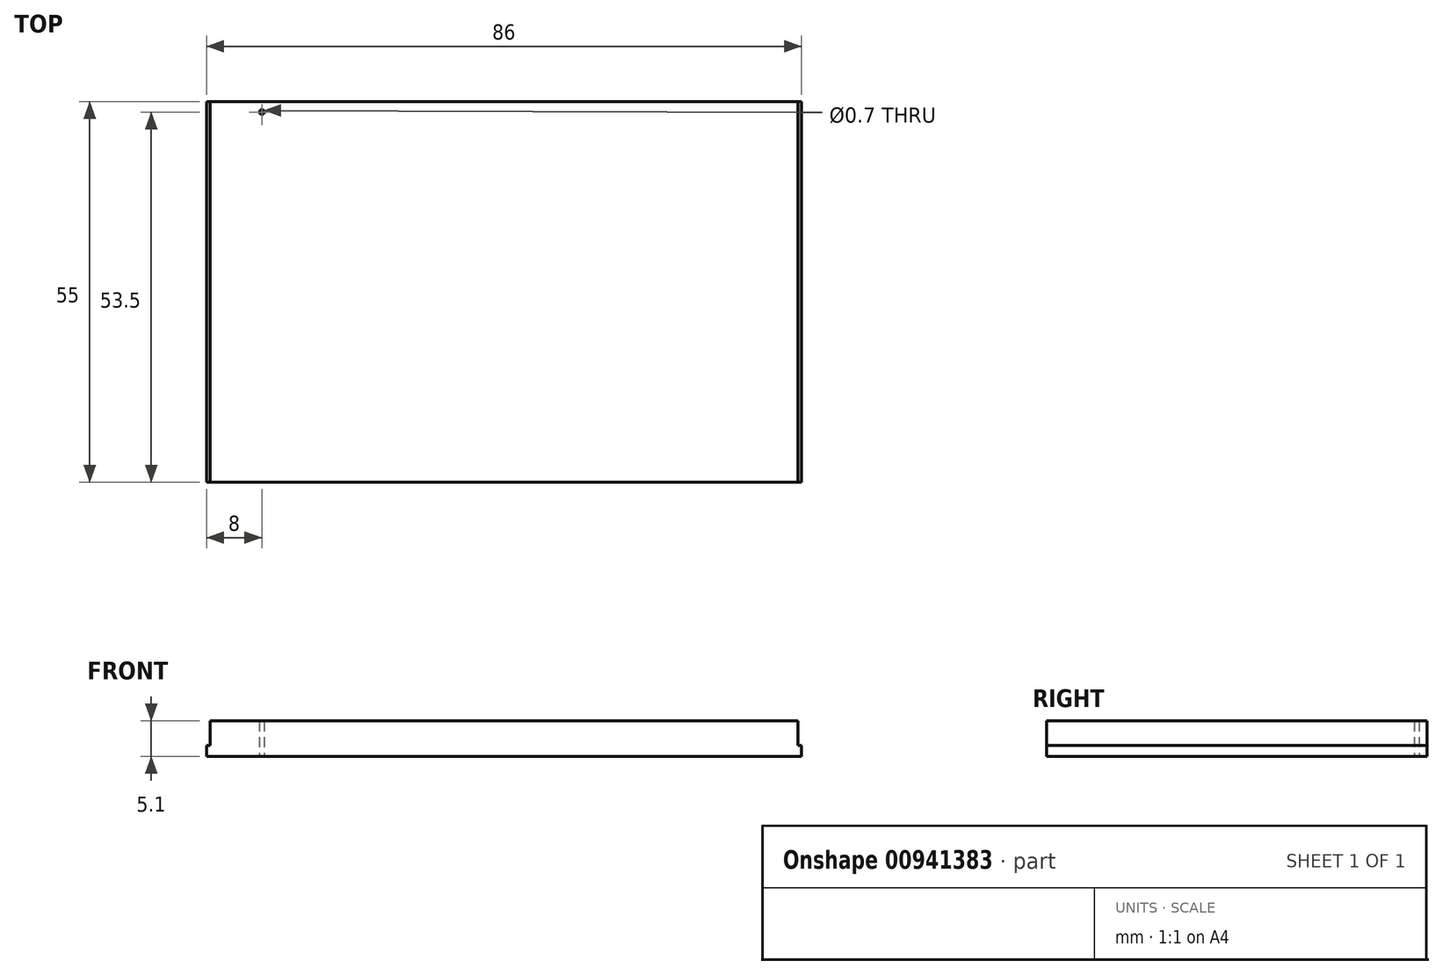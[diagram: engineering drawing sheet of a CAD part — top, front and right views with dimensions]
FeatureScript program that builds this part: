
annotation { "Feature Type Name" : "Feature", "Feature Type Description" : "" }
export const myFeature = defineFeature(function(context is Context, id is Id, definition is map)
    precondition{}
    {
        {
            var Q0;
            Q0=qCreatedBy(makeId("Top.planeOp"),FACE);
            var sketch = newSketch(context, id + "F0", { "sketchPlane" : qUnion([Q0])});
            skLineSegment(sketch, "E0.bottom", {"start": v(43, 27.5) * mm, "end": v(-43, 27.5) * mm});
            skLineSegment(sketch, "E0.top", {"start": v(43, -27.5) * mm, "end": v(-43, -27.5) * mm});
            skLineSegment(sketch, "E0.left", {"start": v(43, 27.5) * mm, "end": v(43, -27.5) * mm});
            skLineSegment(sketch, "E0.right", {"start": v(-43, 27.5) * mm, "end": v(-43, -27.5) * mm});
            skPoint(sketch, "E0.middle", {"position": v(0, 0) * mm});
            skPoint(sketch, "E1", {"position": v(-35, 26) * mm});
            skCircle(sketch, "E2", {"center": v(-35, 26) * mm, "radius": 0.35 * mm});
            skSolve(sketch);
        }
        {
            var Q0;
            Q0=makeQuery(id+"F0.imprint","IMPRINT",FACE,{"disambiguationData":[TD([[makeQuery(id+"F0.imprint","IMPRINT",EDGE,{"derivedFrom":sQuery(id+"F0.wireOp",EDGE,"E0.bottom")}),1.0]])]});
            extrude(context, id + "F1", {"entities" : qUnion([Q0]), "depth" : 1.6 * mm, "offsetDistance" : 25 * mm});
        }
        {
            var Q0;
            Q0=makeQuery(id+"F1.opExtrude","CAP_FACE",FACE,{"disambiguationData":[OSD([sQuery(id+"F0.wireOp",EDGE,"E0.bottom"),sQuery(id+"F0.wireOp",EDGE,"E0.top"),sQuery(id+"F0.wireOp",EDGE,"E0.left"),sQuery(id+"F0.wireOp",EDGE,"E0.right"),sQuery(id+"F0.wireOp",EDGE,"E2")])],"isStart":true});
            var sketch = newSketch(context, id + "F2", { "sketchPlane" : qUnion([Q0])});
            skLineSegment(sketch, "E3.bottom", {"start": v(-42.5, 27.5) * mm, "end": v(42.5, 27.5) * mm});
            skLineSegment(sketch, "E3.top", {"start": v(-42.5, -27.5) * mm, "end": v(42.5, -27.5) * mm});
            skLineSegment(sketch, "E3.left", {"start": v(-42.5, 27.5) * mm, "end": v(-42.5, -27.5) * mm});
            skLineSegment(sketch, "E3.right", {"start": v(42.5, 27.5) * mm, "end": v(42.5, -27.5) * mm});
            skPoint(sketch, "E3.middle", {"position": v(0, 0) * mm});
            skSolve(sketch);
        }
        {
            var Q0;
            Q0=makeQuery(id+"F2.imprint","IMPRINT",FACE,{"disambiguationData":[TD([[makeQuery(id+"F2.imprint","IMPRINT",EDGE,{"derivedFrom":sQuery(id+"F2.wireOp",EDGE,"E3.bottom")}),1.0]])]});
            extrude(context, id + "F3", {"entities" : qUnion([Q0]), "operationType" : NewBodyOperationType.ADD, "oppositeDirection" : true, "depth" : 5.1 * mm, "offsetDistance" : 25 * mm});
        }
    });
